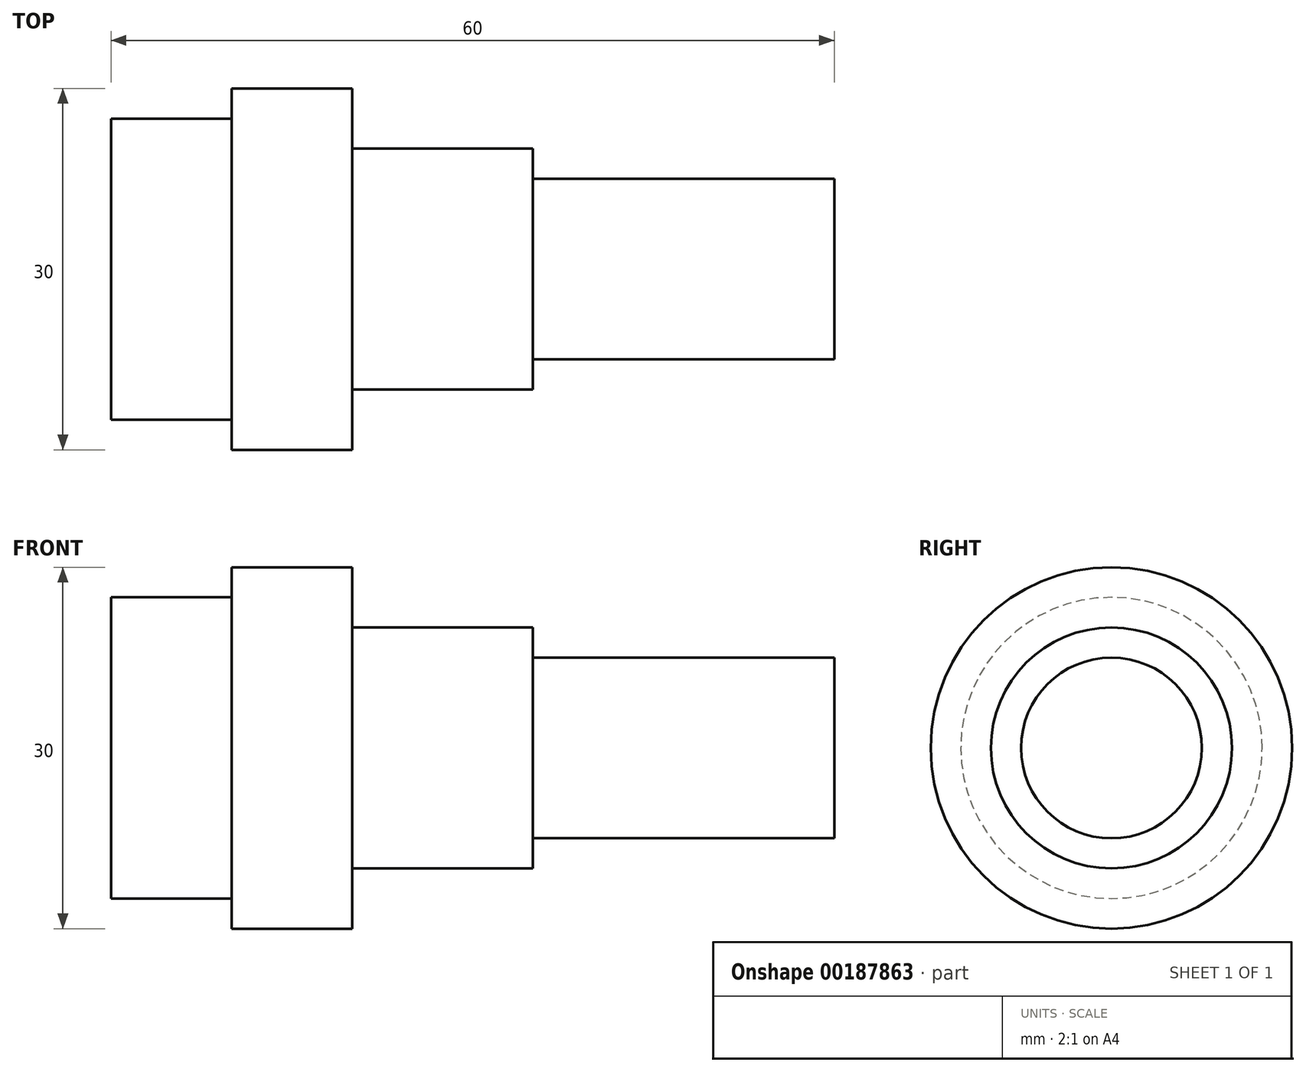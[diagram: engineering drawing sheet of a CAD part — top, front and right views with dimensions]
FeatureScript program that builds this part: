
annotation { "Feature Type Name" : "Feature", "Feature Type Description" : "" }
export const myFeature = defineFeature(function(context is Context, id is Id, definition is map)
    precondition{}
    {
        {
            var Q0;
            Q0=qCreatedBy(makeId("Front.planeOp"),FACE);
            var sketch = newSketch(context, id + "F0", { "sketchPlane" : qUnion([Q0])});
            skLineSegment(sketch, "E0", {"start": v(0, 0) * mm, "end": v(0, 7.5) * mm});
            skLineSegment(sketch, "E1", {"start": v(0, 7.5) * mm, "end": v(-25, 7.5) * mm});
            skLineSegment(sketch, "E2", {"start": v(-25, 7.5) * mm, "end": v(-25, 10) * mm});
            skLineSegment(sketch, "E3", {"start": v(-25, 10) * mm, "end": v(-40, 10) * mm});
            skLineSegment(sketch, "E4", {"start": v(-40, 10) * mm, "end": v(-40, 15) * mm});
            skLineSegment(sketch, "E5", {"start": v(-40, 15) * mm, "end": v(-50, 15) * mm});
            skLineSegment(sketch, "E6", {"start": v(-50, 15) * mm, "end": v(-50, 12.5) * mm});
            skLineSegment(sketch, "E7", {"start": v(-50, 12.5) * mm, "end": v(-60, 12.5) * mm});
            skLineSegment(sketch, "E8", {"start": v(-60, 12.5) * mm, "end": v(-60, 0) * mm});
            skLineSegment(sketch, "E9", {"start": v(-60, 0) * mm, "end": v(0, 0) * mm});
            skLineSegment(sketch, "E10", {"start": v(5.58, 0) * mm, "end": v(-68.62, 0) * mm, "construction": true});
            skSolve(sketch);
        }
        {
            var Q0;
            Q0 = qSketchRegion(id + "F0", true);
            var Q1;
            Q1=sQuery(id+"F0.wireOp",EDGE,"E9");
            revolve(context, id + "F1", {"entities" : qUnion([Q0]), "axis" : qUnion([Q1]), "revolveType" : RevolveType.FULL});
        }
    });
